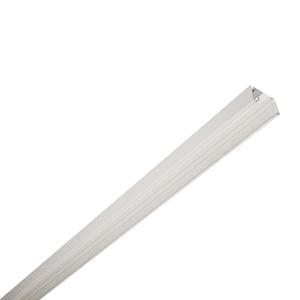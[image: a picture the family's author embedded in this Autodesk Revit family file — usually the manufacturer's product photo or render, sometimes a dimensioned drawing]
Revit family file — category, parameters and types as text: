
# Revit family: 3f_filippi_-_3f_linux_s-nl_ip40_3f_filippi_-_a20012_-_3f_linux_s_nl_l1778
name_source: partatom
category: Lighting Fixtures
units: mm (PartAtom-declared; Revit-internal decimal feet)

## family parameters
Cut with Voids When Loaded = No
Host = Face
Light Source = No
Part Type = Normal
Room Calculation Point = No
Round Connector Dimension = Use Diameter
Shared = No

## types (1)
- 3F Filippi - 3F Linux S-NL IP40
    Apparent Load = 0 VA
    Default Elevation = 1800 mm
    Description = Supporting structure WITHOUT power supply line for continuous channels, suitable for transporting power lines or mounting luminaires.

MECHANICAL
Wired base in hot galvanised steel and painted with polyester base in white colour, obtained through rolling process.
Saline-mist resistance equal to 500hrs and damp resistance equal to 700hrs.
Polycarbonate reinforced cable supports (for use every 500 mm approx.).
Dimensions: 1778x62 mm, height 38 mm. Weight 1.57 kg.
IP40 protection degree.

ELECTRICAL
Feeding input on top (at the beginning or in the middle of the structure).

INSTALLATION
Suspended.
All accessories dedicated to this product are available on the Catalog and on our website www.3F-Filippi.com.

WARNING
Luminaire designed for disposal/recycling at end-of-life.
    Height = 38 mm
    Lamp = 0 x
    Length = 1778 mm
    Luminous efficacy = 0 lm/W
    Manufacturer = 3F Filippi
    ModVariant = No
    Model = 3F Filippi - A20012 - 3F Linux S NL L1778
    Mounting Place = Ceiling
    Mounting Type = Pendant
    Number of Poles = 1
    OnlyDefault = Yes
    Power Factor = 1
    Product Name = 3F Filippi - 3F Linux S-NL IP40
    Product group = Accessories
    ProductGroupID = 98
    Protection Class = Protection class
    Protection Degree = IP 40
    RLX_Detail_Level = 1
    RLX_Emergency_Light_Flux = 0 lm
    RLX_Emergency_Type = 0
    RLX_Emergency_Type_DB = No
    RlxData = <blob elided: 29041 chars, md5=ac473d79>
    Standby Power = 0 W
    System Light Flux = 0 lm
    System Power = 0 W
    Type Comments = Product without accessories
    Type Image = 3ffilippi_3f_linux_s-n_ip40_l1778.jpg
    URL = http://relux.com
    VarID = ---
    Voltage = 0 V
    Weight = 0.00 kg
    Width = 62 mm  [stored 0.203412 ft]

note: [stored X ft] marks values corroborated as IEEE doubles in the binary element streams (Revit-internal decimal feet)

## geometry (parser evidence)
native form markers: Blend x4, Sweep x11
no freeform markers — native parametric forms only
